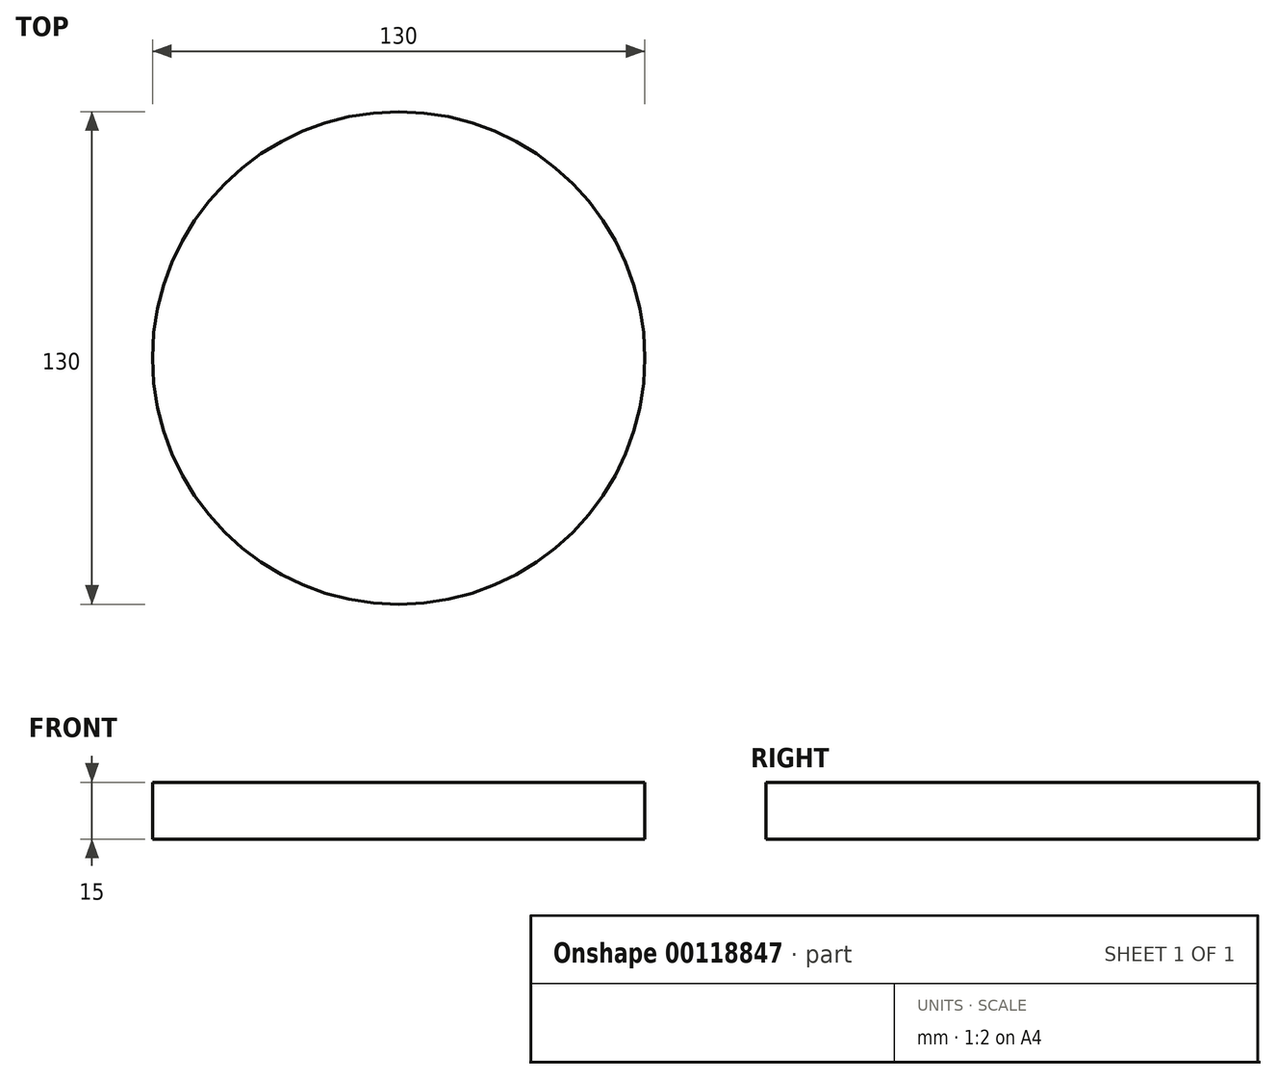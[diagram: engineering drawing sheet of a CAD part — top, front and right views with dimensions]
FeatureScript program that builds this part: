
annotation { "Feature Type Name" : "Feature", "Feature Type Description" : "" }
export const myFeature = defineFeature(function(context is Context, id is Id, definition is map)
    precondition{}
    {
        {
            var Q0;
            Q0=qCreatedBy(makeId("Top.planeOp"),FACE);
            var sketch = newSketch(context, id + "F0", { "sketchPlane" : qUnion([Q0])});
            skCircle(sketch, "E0", {"center": v(-85.62, 19.67) * mm, "radius": 65 * mm});
            skSolve(sketch);
        }
        {
            var Q0;
            Q0=makeQuery(id+"F0.imprint","IMPRINT",FACE,{"disambiguationData":[TD([[makeQuery(id+"F0.imprint","IMPRINT",EDGE,{"derivedFrom":sQuery(id+"F0.wireOp",EDGE,"E0")}),1.0]])]});
            extrude(context, id + "F1", {"entities" : qUnion([Q0]), "depth" : 15 * mm});
        }
    });
